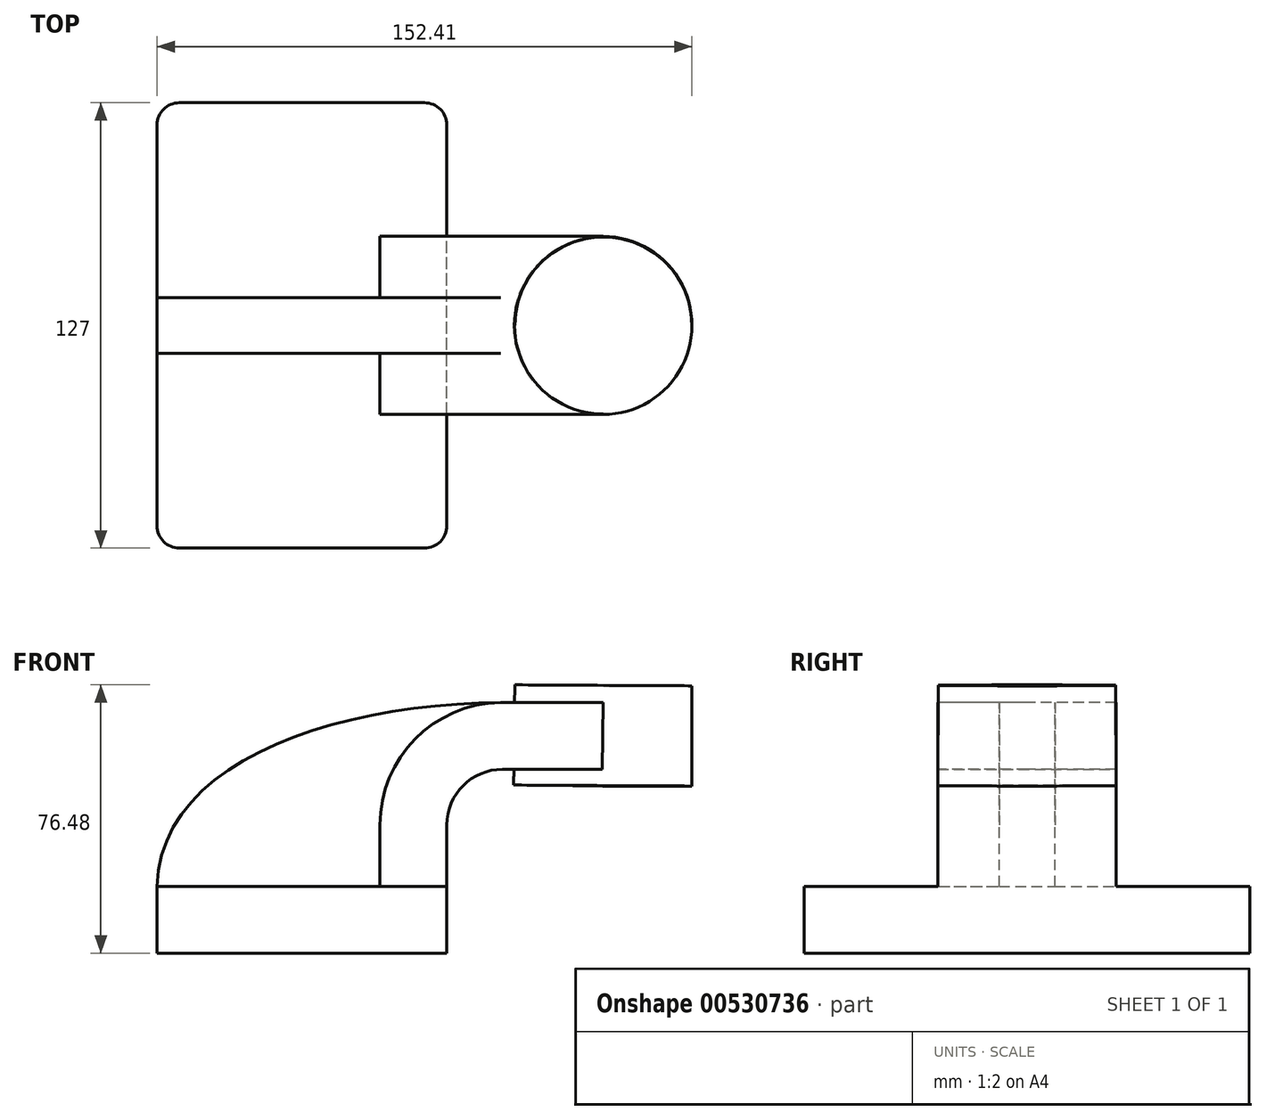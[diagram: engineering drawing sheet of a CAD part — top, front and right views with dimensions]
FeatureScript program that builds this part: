
annotation { "Feature Type Name" : "Feature", "Feature Type Description" : "" }
export const myFeature = defineFeature(function(context is Context, id is Id, definition is map)
    precondition{}
    {
        {
            var Q0;
            Q0=qCreatedBy(makeId("Front.planeOp"),FACE);
            var sketch = newSketch(context, id + "F0", { "sketchPlane" : qUnion([Q0])});
            skLineSegment(sketch, "E0.bottom", {"start": v(41.28, -9.52) * mm, "end": v(-41.28, -9.52) * mm});
            skLineSegment(sketch, "E0.top", {"start": v(41.27, 9.53) * mm, "end": v(-41.28, 9.53) * mm});
            skLineSegment(sketch, "E0.left", {"start": v(41.28, -9.52) * mm, "end": v(41.28, 9.53) * mm});
            skLineSegment(sketch, "E0.right", {"start": v(-41.28, -9.52) * mm, "end": v(-41.28, 9.53) * mm});
            skPoint(sketch, "E0.middle", {"position": v(0, 0) * mm});
            skLineSegment(sketch, "E1.bottom", {"start": v(111.12, 38.1) * mm, "end": v(60.33, 38.1) * mm});
            skLineSegment(sketch, "E1.top", {"start": v(111.12, 66.68) * mm, "end": v(60.33, 66.68) * mm});
            skLineSegment(sketch, "E1.left", {"start": v(111.12, 38.1) * mm, "end": v(111.12, 66.68) * mm});
            skLineSegment(sketch, "E1.right", {"start": v(60.33, 38.1) * mm, "end": v(60.33, 66.68) * mm});
            skPoint(sketch, "E1.middle", {"position": v(85.72, 52.39) * mm});
            skLineSegment(sketch, "E2", {"start": v(41.27, 9.53) * mm, "end": v(41.27, 27) * mm});
            skArc(sketch, "E3", {"start": v(41.27, 27) * mm, "mid": v(45.92, 38.23) * mm, "end": v(57.15, 42.88) * mm});
            skLineSegment(sketch, "E4", {"start": v(57.15, 42.88) * mm, "end": v(85.5, 42.88) * mm});
            skLineSegment(sketch, "E5.0", {"start": v(57.15, 61.93) * mm, "end": v(85.88, 61.93) * mm});
            skArc(sketch, "E5.1", {"start": v(22.23, 27) * mm, "mid": v(32.45, 51.7) * mm, "end": v(57.15, 61.93) * mm});
            skLineSegment(sketch, "E5.2", {"start": v(22.22, 9.53) * mm, "end": v(22.22, 27) * mm});
            skLineSegment(sketch, "E6", {"start": v(85.5, 42.88) * mm, "end": v(85.88, 66.68) * mm});
            skFitSpline(sketch, "E7", {"points": [v(-41.28, 9.53) * mm, v(57.15, 61.93) * mm], "startDerivative": vector(2.63, 106.95) * mm, "endDerivative": vector(143.57, 0.93) * mm});
            skLineSegment(sketch, "E8", {"start": v(85.72, 38.1) * mm, "end": v(85.88, 66.68) * mm});
            skSolve(sketch);
        }
        {
            var Q0;
            Q0=makeQuery(id+"F0.imprint","IMPRINT",FACE,{"disambiguationData":[TD([[makeQuery(id+"F0.imprint","IMPRINT",EDGE,{"derivedFrom":sQuery(id+"F0.wireOp",EDGE,"E0.bottom")}),-1.0]])]});
            extrude(context, id + "F1", {"entities" : qUnion([Q0]), "endBound" : BoundingType.SYMMETRIC, "depth" : 127 * mm, "offsetDistance" : 25.4 * mm});
        }
        {
            var Q0;
            {var subQ1=sQuery(id+"F0.wireOp",EDGE,"E2");Q0=makeQuery(id+"F0.imprint","IMPRINT",FACE,{"disambiguationData":[TD([[makeQuery(id+"F0.imprint","IMPRINT",EDGE,{"derivedFrom":subQ1}),1.0]])]});}
            var Q1;
            {var subQ0=sQuery(id+"F0.wireOp",EDGE,"E4");var subQ1=sQuery(id+"F0.wireOp",EDGE,"E1.right");var subQ2=makeQuery(id+"F0.imprint","INTERSECT",VERTEX,{"derivedFrom":[subQ1,subQ0]});Q1=makeQuery(id+"F0.imprint","IMPRINT",FACE,{"disambiguationData":[TD([[makeQuery(id+"F0.imprint","IMPRINT",EDGE,{"disambiguationData":[TD([[subQ2,-1.0]])],"derivedFrom":subQ1}),-1.0]])]});}
            extrude(context, id + "F2", {"entities" : qUnion([Q0, Q1]), "operationType" : NewBodyOperationType.ADD, "endBound" : BoundingType.SYMMETRIC, "depth" : 50.8 * mm, "offsetDistance" : 25.4 * mm});
        }
        {
            var Q0;
            {var subQ3=sQuery(id+"F0.wireOp",EDGE,"E5.2");Q0=makeQuery(id+"F0.imprint","IMPRINT",FACE,{"disambiguationData":[TD([[makeQuery(id+"F0.imprint","IMPRINT",EDGE,{"derivedFrom":subQ3}),1.0]])]});}
            extrude(context, id + "F3", {"entities" : qUnion([Q0]), "operationType" : NewBodyOperationType.ADD, "endBound" : BoundingType.SYMMETRIC, "depth" : 15.88 * mm, "offsetDistance" : 25.4 * mm});
        }
        {
            var Q0;
            {var subQ0=sQuery(id+"F0.wireOp",EDGE,"E1.left");Q0=makeQuery(id+"F0.imprint","IMPRINT",FACE,{"disambiguationData":[TD([[makeQuery(id+"F0.imprint","IMPRINT",EDGE,{"derivedFrom":subQ0}),1.0]])]});}
            var Q1;
            Q1=sQuery(id+"F0.wireOp",EDGE,"E8");
            revolve(context, id + "F4", {"operationType" : NewBodyOperationType.ADD, "entities" : qUnion([Q0]), "axis" : qUnion([Q1]), "revolveType" : RevolveType.FULL});
        }
        {
            var Q0;
            Q0=makeQuery(id+"F1.opExtrude","CAP_EDGE",EDGE,{"disambiguationData":[OSD([sQuery(id+"F0.wireOp",EDGE,"E0.left")])],"isStart":false});
            var Q1;
            Q1=makeQuery(id+"F1.opExtrude","CAP_EDGE",EDGE,{"disambiguationData":[OSD([sQuery(id+"F0.wireOp",EDGE,"E0.right")])],"isStart":false});
            var Q2;
            Q2=makeQuery(id+"F1.opExtrude","CAP_EDGE",EDGE,{"disambiguationData":[OSD([sQuery(id+"F0.wireOp",EDGE,"E0.right")])],"isStart":true});
            var Q3;
            Q3=makeQuery(id+"F1.opExtrude","CAP_EDGE",EDGE,{"disambiguationData":[OSD([sQuery(id+"F0.wireOp",EDGE,"E0.left")])],"isStart":true});
            fillet(context, id + "F5", {"entities" : qUnion([Q0, Q1, Q2, Q3]), "radius" : 6.35 * mm, "tangentPropagation" : true, "allowEdgeOverflow" : false});
        }
    });
